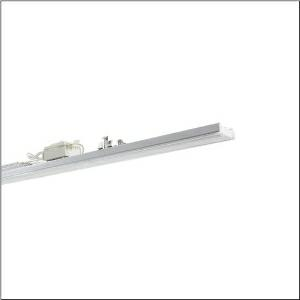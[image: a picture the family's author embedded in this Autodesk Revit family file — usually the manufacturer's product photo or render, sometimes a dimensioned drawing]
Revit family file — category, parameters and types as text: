
# Revit family: licross_r__11_recessed_ho_51tl12mv4hxm_54da
name_source: partatom
category: Lighting Fixtures
units: mm (PartAtom-declared; Revit-internal decimal feet)

## family parameters
Cut with Voids When Loaded = No
Host = Face
Light Source = No
Part Type = Normal
Room Calculation Point = No
Round Connector Dimension = Use Diameter
Shared = No

## types (1)
- --- (1 x LED, 17260 lm, 89.2 W, 4000K)
    Apparent Load = 89 VA
    CIE Flux Codes = 66 91 98 100 100
    Color Rendering = 80
    Color Temperature = 4000K
    Default Elevation = 1800 mm
    Description = Licross® 11 Recessed HO, luminaire insert, of sheet steel, coil coated, white, length: 2.250mm, width: 66mm, height: 67mm, LED rated luminous flux: 17.270lm, light colour: 840, control gear: ON/OFF Multilumen, with plug, 3-pole, with phase selection, mains connection: 220..240V, AC, 50/60Hz, rated input power: 89W, halogen-free wiring, primary optical cover: cover, of PMMA, light emission: direct distribution, primary light characteristic: symmetric, protection rating (complete): IP40, insulation class (complete): insulation class I (protective earthing), certification: CE, ENEC, VDE, UKCA, protection symbol: D if used in an environment without relevant dust loads with corresponding accessories, impact resistance: IK06, permissible ambient temperature for indoor applications: -35..+35°C, corresponds to IFS (International Featured Standards) requirements for safety and quality in the food industry, reducing of maximum allowable ambient temperature of 5°C with ceiling mounting, LABS conformity tested according to VDMA 24364:2018-05, packaging unit: 1 piece
    Height = 58 mm
    Lamp = 1 x LED
    Lamp Light Flux = 17260 lm
    Lamp Power = 89.2 W
    Lamp count = 1
    Length = 2250 mm
    Luminous efficacy = 194 lm/W
    Manufacturer = Siteco
    ModVariant = No
    Model = 51TL12MV4HXM
    Mounting Place = Ceiling
    Mounting Type = Pendant
    Number of Poles = 1
    OnlyDefault = Yes
    Power Factor = 1
    Product Name = Licross® 11 Recessed HO
    Product group = luminaire insert
    ProductGroupID = 902
    Protection Class = Protection class I
    Protection Degree = IP 40
    RLX_Detail_Level = 1
    RLX_Emergency_Light_Flux = 0 lm
    RLX_Emergency_Type = 0
    RLX_Emergency_Type_DB = No
    RlxData = <blob elided: 27033 chars, md5=cfd2453f>
    Socket = socket
    Standby Power = 0 W
    System Light Flux = 17260 lm
    System Power = 89 W
    Type Comments = factory setting: luminous flux: 100 % | (A | C | E) | 210 mA
    Type Image = l_1296930.jpg
    URL = http://relux.com
    VarID = @adj_085090
    Voltage = 0 V
    Weight = 0.00 kg
    Width = 66 mm

## geometry (parser evidence)
native form markers: Blend x4, Sweep x10
no freeform markers — native parametric forms only
